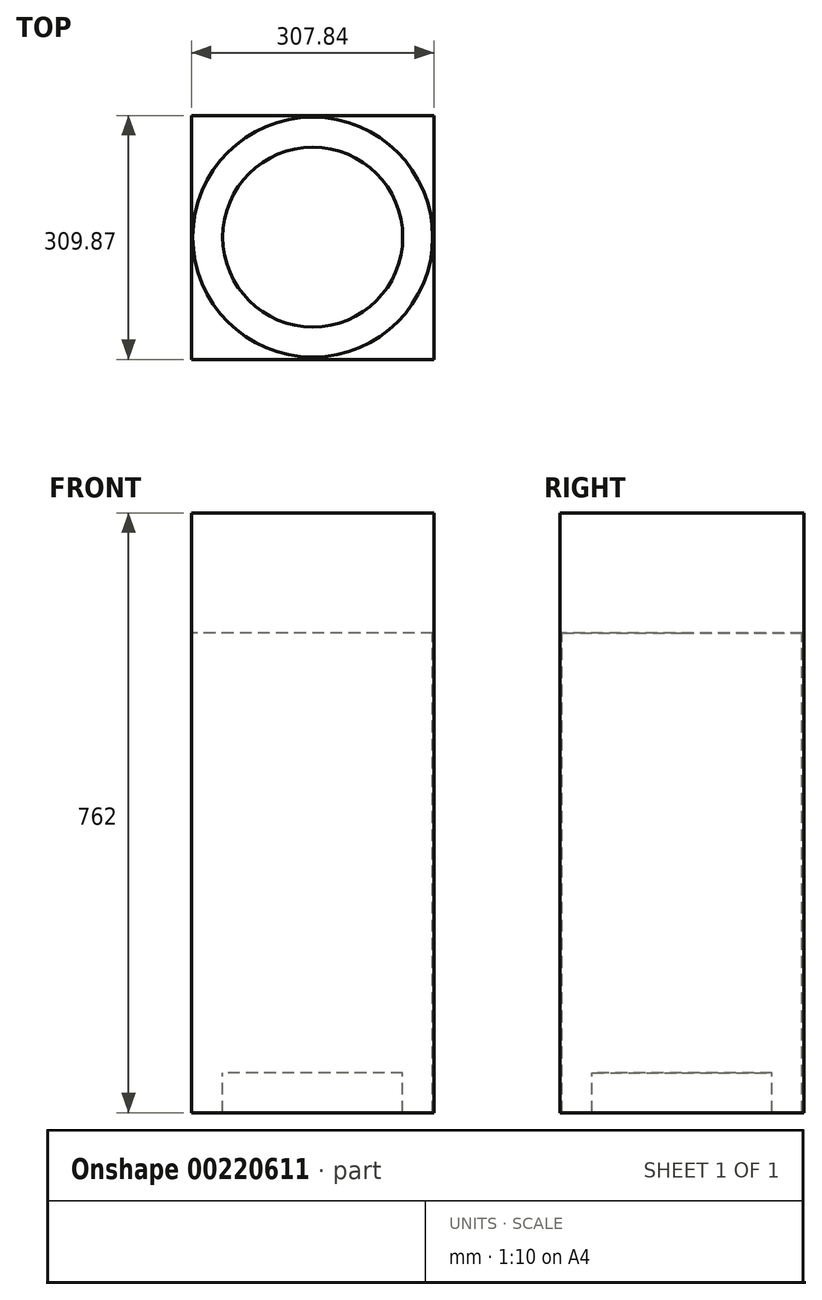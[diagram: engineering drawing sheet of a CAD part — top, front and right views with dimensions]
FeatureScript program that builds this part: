
annotation { "Feature Type Name" : "Feature", "Feature Type Description" : "" }
export const myFeature = defineFeature(function(context is Context, id is Id, definition is map)
    precondition{}
    {
        {
            var Q0;
            Q0=qCreatedBy(makeId("Top.planeOp"),FACE);
            var sketch = newSketch(context, id + "F0", { "sketchPlane" : qUnion([Q0])});
            skCircle(sketch, "E0", {"center": v(0, 0) * mm, "radius": 114.3 * mm});
            skSolve(sketch);
        }
        {
            var Q0;
            Q0=sQuery(id+"F0.wireOp",EDGE,"E0");
            extrude(context, id + "F1", {"bodyType" : ToolBodyType.SURFACE, "surfaceEntities" : qUnion([Q0]), "depth" : 50.8 * mm});
        }
        {
            var Q0;
            Q0=qCreatedBy(makeId("Top.planeOp"),FACE);
            var sketch = newSketch(context, id + "F2", { "sketchPlane" : qUnion([Q0])});
            skCircle(sketch, "E1", {"center": v(0, 0) * mm, "radius": 152.4 * mm});
            skSolve(sketch);
        }
        {
            var Q0;
            Q0=sQuery(id+"F2.wireOp",EDGE,"E1");
            extrude(context, id + "F3", {"bodyType" : ToolBodyType.SURFACE, "surfaceEntities" : qUnion([Q0]), "depth" : 609.6 * mm});
        }
        {
            var Q0;
            Q0=qCreatedBy(makeId("Top.planeOp"),FACE);
            var sketch = newSketch(context, id + "F4", { "sketchPlane" : qUnion([Q0])});
            skFitSpline(sketch, "E2", {"points": [v(-166.8, 69.84) * mm, v(-97.64, 44.75) * mm, v(-42.72, 89.5) * mm, v(78.65, 65.1) * mm, v(85.43, -56.28) * mm, v(26.44, -92.21) * mm, v(-67.8, -70.52) * mm, v(-95.6, 13.56) * mm, v(-6.78, 50.18) * mm, v(35.26, -38.65) * mm, v(-41.36, -20.34) * mm], "startDerivative": vector(847.03, -516.86) * mm, "endDerivative": vector(-1084.95, 534.82) * mm});
            skSolve(sketch);
        }
        {
            var Q0;
            Q0=qCreatedBy(makeId("Top.planeOp"),FACE);
            var sketch = newSketch(context, id + "F5", { "sketchPlane" : qUnion([Q0])});
            skLineSegment(sketch, "E3.bottom", {"start": v(-153.92, 154.6) * mm, "end": v(153.92, 154.6) * mm});
            skLineSegment(sketch, "E3.top", {"start": v(-153.92, -155.27) * mm, "end": v(153.92, -155.27) * mm});
            skLineSegment(sketch, "E3.left", {"start": v(-153.92, 154.6) * mm, "end": v(-153.92, -155.27) * mm});
            skLineSegment(sketch, "E3.right", {"start": v(153.92, 154.6) * mm, "end": v(153.92, -155.27) * mm});
            skSolve(sketch);
        }
        {
            var Q0;
            Q0=sQuery(id+"F5.wireOp",EDGE,"E3.top");
            var Q1;
            Q1=sQuery(id+"F5.wireOp",EDGE,"E3.left");
            var Q2;
            Q2=sQuery(id+"F5.wireOp",EDGE,"E3.bottom");
            var Q3;
            Q3=sQuery(id+"F5.wireOp",EDGE,"E3.right");
            extrude(context, id + "F6", {"bodyType" : ToolBodyType.SURFACE, "surfaceEntities" : qUnion([Q0, Q1, Q2, Q3]), "depth" : 762 * mm});
        }
    });
